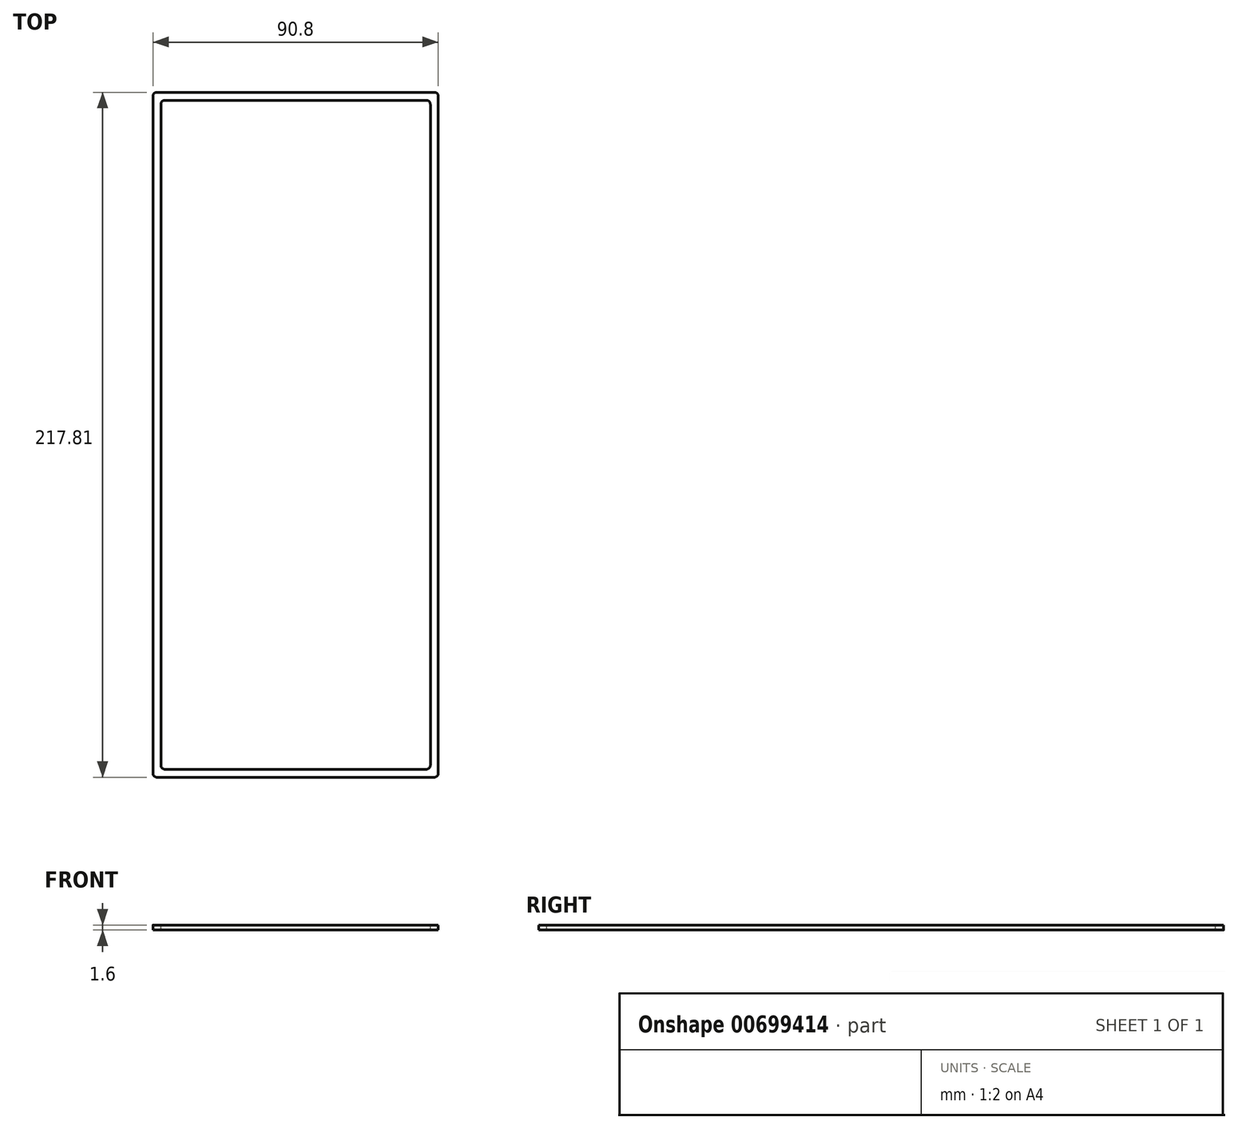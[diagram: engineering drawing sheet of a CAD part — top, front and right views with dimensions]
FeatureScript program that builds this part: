
annotation { "Feature Type Name" : "Feature", "Feature Type Description" : "" }
export const myFeature = defineFeature(function(context is Context, id is Id, definition is map)
    precondition{}
    {
        {
            assignVariable(context, id + "F0", {"name" : "BOXHEIGHT", "anyValue" : 1.6});
        }
        {
            var Q0;
            Q0=qCreatedBy(makeId("Top.planeOp"),FACE);
            var sketch = newSketch(context, id + "F1", { "sketchPlane" : qUnion([Q0])});
            skLineSegment(sketch, "E0.bottom", {"start": v(1.27, 0) * mm, "end": v(89.53, 0) * mm});
            skLineSegment(sketch, "E0.top", {"start": v(1.27, 217.8) * mm, "end": v(89.53, 217.8) * mm});
            skLineSegment(sketch, "E0.left", {"start": v(0, 1.27) * mm, "end": v(0, 216.53) * mm});
            skLineSegment(sketch, "E0.right", {"start": v(90.8, 1.27) * mm, "end": v(90.8, 216.54) * mm});
            skPoint(sketch, "E1.visualSharp", {"position": v(0, 217.8) * mm});
            skArc(sketch, "E1.filletArc", {"start": v(1.27, 217.8) * mm, "mid": v(0.37, 217.43) * mm, "end": v(0, 216.53) * mm});
            skPoint(sketch, "E2.visualSharp", {"position": v(90.8, 217.8) * mm});
            skArc(sketch, "E2.filletArc", {"start": v(90.8, 216.54) * mm, "mid": v(90.43, 217.43) * mm, "end": v(89.53, 217.8) * mm});
            skPoint(sketch, "E3.visualSharp", {"position": v(90.8, 0) * mm});
            skArc(sketch, "E3.filletArc", {"start": v(89.53, 0) * mm, "mid": v(90.43, 0.37) * mm, "end": v(90.8, 1.27) * mm});
            skPoint(sketch, "E4.visualSharp", {"position": v(0, 0) * mm});
            skArc(sketch, "E4.filletArc", {"start": v(0, 1.27) * mm, "mid": v(0.37, 0.37) * mm, "end": v(1.27, 0) * mm});
            skSolve(sketch);
        }
        {
            var Q0;
            Q0 = qSketchRegion(id + "F1", true);
            extrude(context, id + "F2", {"entities" : qUnion([Q0]), "depth" : (getVariable(context, 'BOXHEIGHT')) * mm, "offsetDistance" : 25.4 * mm});
        }
        {
            var Q0;
            Q0=makeQuery(id+"F2.opExtrude","CAP_FACE",FACE,{"disambiguationData":[OSD([sQuery(id+"F1.wireOp",EDGE,"E0.bottom"),sQuery(id+"F1.wireOp",EDGE,"E0.top"),sQuery(id+"F1.wireOp",EDGE,"E0.left"),sQuery(id+"F1.wireOp",EDGE,"E0.right")])],"isStart":false});
            var sketch = newSketch(context, id + "F3", { "sketchPlane" : qUnion([Q0])});
            skLineSegment(sketch, "E5.0", {"start": v(2.54, 3.81) * mm, "end": v(2.54, 214) * mm});
            skLineSegment(sketch, "E5.1", {"start": v(3.81, 2.54) * mm, "end": v(87, 2.54) * mm});
            skLineSegment(sketch, "E5.2", {"start": v(88.27, 3.81) * mm, "end": v(88.27, 214) * mm});
            skLineSegment(sketch, "E5.3", {"start": v(3.81, 215.27) * mm, "end": v(87, 215.27) * mm});
            skPoint(sketch, "E6.visualSharp", {"position": v(2.54, 215.27) * mm});
            skArc(sketch, "E6.filletArc", {"start": v(3.81, 215.27) * mm, "mid": v(2.91, 214.9) * mm, "end": v(2.54, 214) * mm});
            skPoint(sketch, "E7.visualSharp", {"position": v(88.27, 215.27) * mm});
            skArc(sketch, "E7.filletArc", {"start": v(88.27, 214) * mm, "mid": v(87.9, 214.9) * mm, "end": v(87, 215.27) * mm});
            skPoint(sketch, "E8.visualSharp", {"position": v(88.27, 2.54) * mm});
            skArc(sketch, "E8.filletArc", {"start": v(87, 2.54) * mm, "mid": v(87.9, 2.91) * mm, "end": v(88.27, 3.81) * mm});
            skPoint(sketch, "E9.visualSharp", {"position": v(2.54, 2.54) * mm});
            skArc(sketch, "E9.filletArc", {"start": v(2.54, 3.81) * mm, "mid": v(2.91, 2.91) * mm, "end": v(3.81, 2.54) * mm});
            skSolve(sketch);
        }
        {
            var Q0;
            Q0 = qSketchRegion(id + "F3", true);
            extrude(context, id + "F4", {"entities" : qUnion([Q0]), "operationType" : NewBodyOperationType.REMOVE, "oppositeDirection" : true, "depth" : ((getVariable(context, 'BOXHEIGHT')) - 0.1) * mm, "offsetDistance" : 25.4 * mm});
        }
    });
